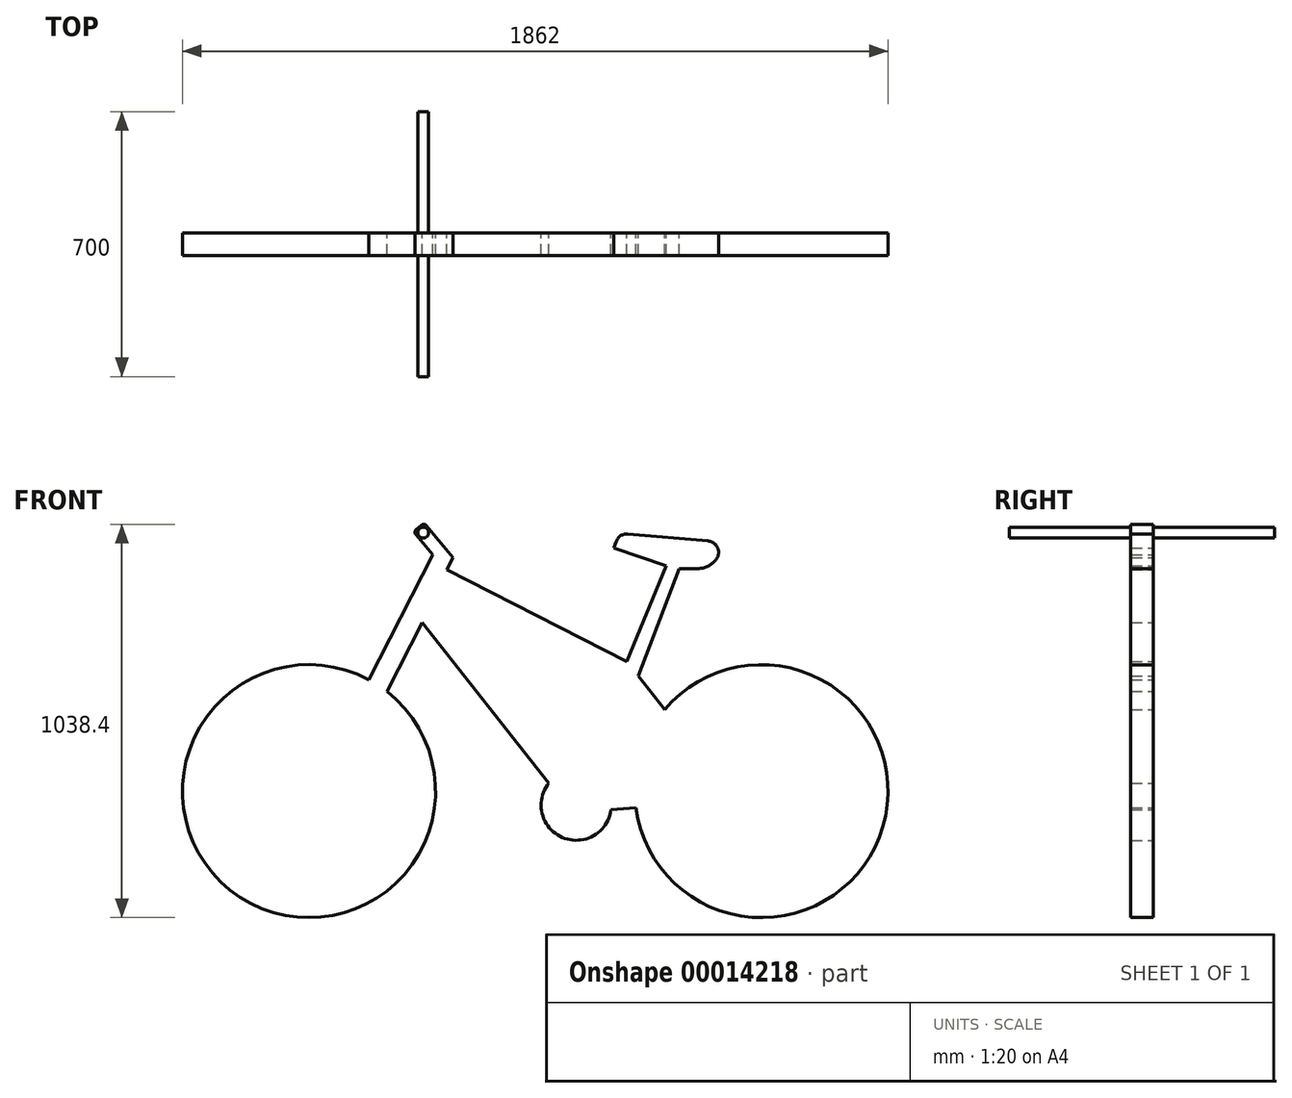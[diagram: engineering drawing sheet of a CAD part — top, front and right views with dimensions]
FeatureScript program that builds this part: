
annotation { "Feature Type Name" : "Feature", "Feature Type Description" : "" }
export const myFeature = defineFeature(function(context is Context, id is Id, definition is map)
    precondition{}
    {
        {
            var Q0;
            Q0=qCreatedBy(makeId("Front.planeOp"),FACE);
            var sketch = newSketch(context, id + "F0", { "sketchPlane" : qUnion([Q0])});
            skArc(sketch, "E0", {"start": v(1690.2, 939.1) * mm, "mid": v(2341.99, 889.68) * mm, "end": v(1765.52, 1197.83) * mm});
            skArc(sketch, "E1", {"start": v(984.67, 1277.64) * mm, "mid": v(645.16, 703.08) * mm, "end": v(1032.87, 1246.28) * mm});
            skArc(sketch, "E2", {"start": v(1460.2, 1004.52) * mm, "mid": v(1495.67, 860.95) * mm, "end": v(1624.34, 933.85) * mm});
            skLineSegment(sketch, "E3", {"start": v(1690.2, 939.1) * mm, "end": v(1624.34, 933.85) * mm});
            skLineSegment(sketch, "E4", {"start": v(1460.2, 1004.52) * mm, "end": v(1126.04, 1428.2) * mm});
            skLineSegment(sketch, "E5", {"start": v(1126.04, 1428.2) * mm, "end": v(1032.87, 1246.28) * mm});
            skLineSegment(sketch, "E6", {"start": v(984.67, 1277.64) * mm, "end": v(1153.42, 1607.15) * mm});
            skLineSegment(sketch, "E7", {"start": v(1153.42, 1607.15) * mm, "end": v(1109.36, 1660.14) * mm});
            skLineSegment(sketch, "E8", {"start": v(1110.65, 1674.22) * mm, "end": v(1123.76, 1685.13) * mm});
            skLineSegment(sketch, "E9", {"start": v(1137.85, 1683.83) * mm, "end": v(1207.8, 1599.71) * mm});
            skLineSegment(sketch, "E10", {"start": v(1207.8, 1599.71) * mm, "end": v(1191.34, 1567.56) * mm});
            skLineSegment(sketch, "E11", {"start": v(1191.34, 1567.56) * mm, "end": v(1665.1, 1324.93) * mm});
            skLineSegment(sketch, "E12", {"start": v(1665.1, 1324.93) * mm, "end": v(1769.6, 1577.53) * mm});
            skLineSegment(sketch, "E13", {"start": v(1769.6, 1577.53) * mm, "end": v(1631.72, 1624.7) * mm});
            skLineSegment(sketch, "E14", {"start": v(1631.72, 1624.7) * mm, "end": v(1637.69, 1642.13) * mm});
            skLineSegment(sketch, "E15", {"start": v(1668.71, 1662.3) * mm, "end": v(1880.71, 1643.58) * mm});
            skLineSegment(sketch, "E16", {"start": v(1901.73, 1595.24) * mm, "end": v(1900.57, 1593.76) * mm});
            skLineSegment(sketch, "E17", {"start": v(1853.26, 1570.67) * mm, "end": v(1804.47, 1570.67) * mm});
            skLineSegment(sketch, "E18", {"start": v(1804.47, 1570.67) * mm, "end": v(1695.82, 1287.08) * mm});
            skLineSegment(sketch, "E19", {"start": v(1695.82, 1287.08) * mm, "end": v(1765.52, 1197.83) * mm});
            skPoint(sketch, "E20.visualSharp", {"position": v(1645.3, 1664.37) * mm});
            skArc(sketch, "E20.filletArc", {"start": v(1668.71, 1662.3) * mm, "mid": v(1649.72, 1657.57) * mm, "end": v(1637.69, 1642.13) * mm});
            skPoint(sketch, "E21.visualSharp", {"position": v(1935.66, 1638.73) * mm});
            skArc(sketch, "E21.filletArc", {"start": v(1901.73, 1595.24) * mm, "mid": v(1905.59, 1625.66) * mm, "end": v(1880.71, 1643.58) * mm});
            skPoint(sketch, "E22.visualSharp", {"position": v(1882.55, 1570.67) * mm});
            skArc(sketch, "E22.filletArc", {"start": v(1853.26, 1570.67) * mm, "mid": v(1879.58, 1576.75) * mm, "end": v(1900.57, 1593.76) * mm});
            skPoint(sketch, "E23.visualSharp", {"position": v(1131.45, 1691.52) * mm});
            skArc(sketch, "E23.filletArc", {"start": v(1137.85, 1683.83) * mm, "mid": v(1131.07, 1687.4) * mm, "end": v(1123.76, 1685.13) * mm});
            skPoint(sketch, "E24.visualSharp", {"position": v(1102.96, 1667.83) * mm});
            skArc(sketch, "E24.filletArc", {"start": v(1110.65, 1674.22) * mm, "mid": v(1107.09, 1667.45) * mm, "end": v(1109.36, 1660.14) * mm});
            skSolve(sketch);
        }
        {
            var Q0;
            Q0=makeQuery(id+"F0.imprint","IMPRINT",FACE,{"disambiguationData":[TD([[makeQuery(id+"F0.imprint","IMPRINT",EDGE,{"derivedFrom":sQuery(id+"F0.wireOp",EDGE,"E0")}),1.0]])]});
            extrude(context, id + "F1", {"entities" : qUnion([Q0]), "endBound" : BoundingType.SYMMETRIC, "depth" : 60 * mm});
        }
        {
            var Q0;
            Q0=qCreatedBy(makeId("Front.planeOp"),FACE);
            var sketch = newSketch(context, id + "F2", { "sketchPlane" : qUnion([Q0])});
            skCircle(sketch, "E25", {"center": v(1128.77, 1665.67) * mm, "radius": 14.32 * mm});
            skSolve(sketch);
        }
        {
            var Q0;
            Q0=makeQuery(id+"F2.imprint","IMPRINT",FACE,{"disambiguationData":[TD([[makeQuery(id+"F2.imprint","IMPRINT",EDGE,{"derivedFrom":sQuery(id+"F2.wireOp",EDGE,"E25")}),1.0]])]});
            extrude(context, id + "F3", {"entities" : qUnion([Q0]), "operationType" : NewBodyOperationType.ADD, "endBound" : BoundingType.SYMMETRIC, "depth" : 700 * mm});
        }
    });
